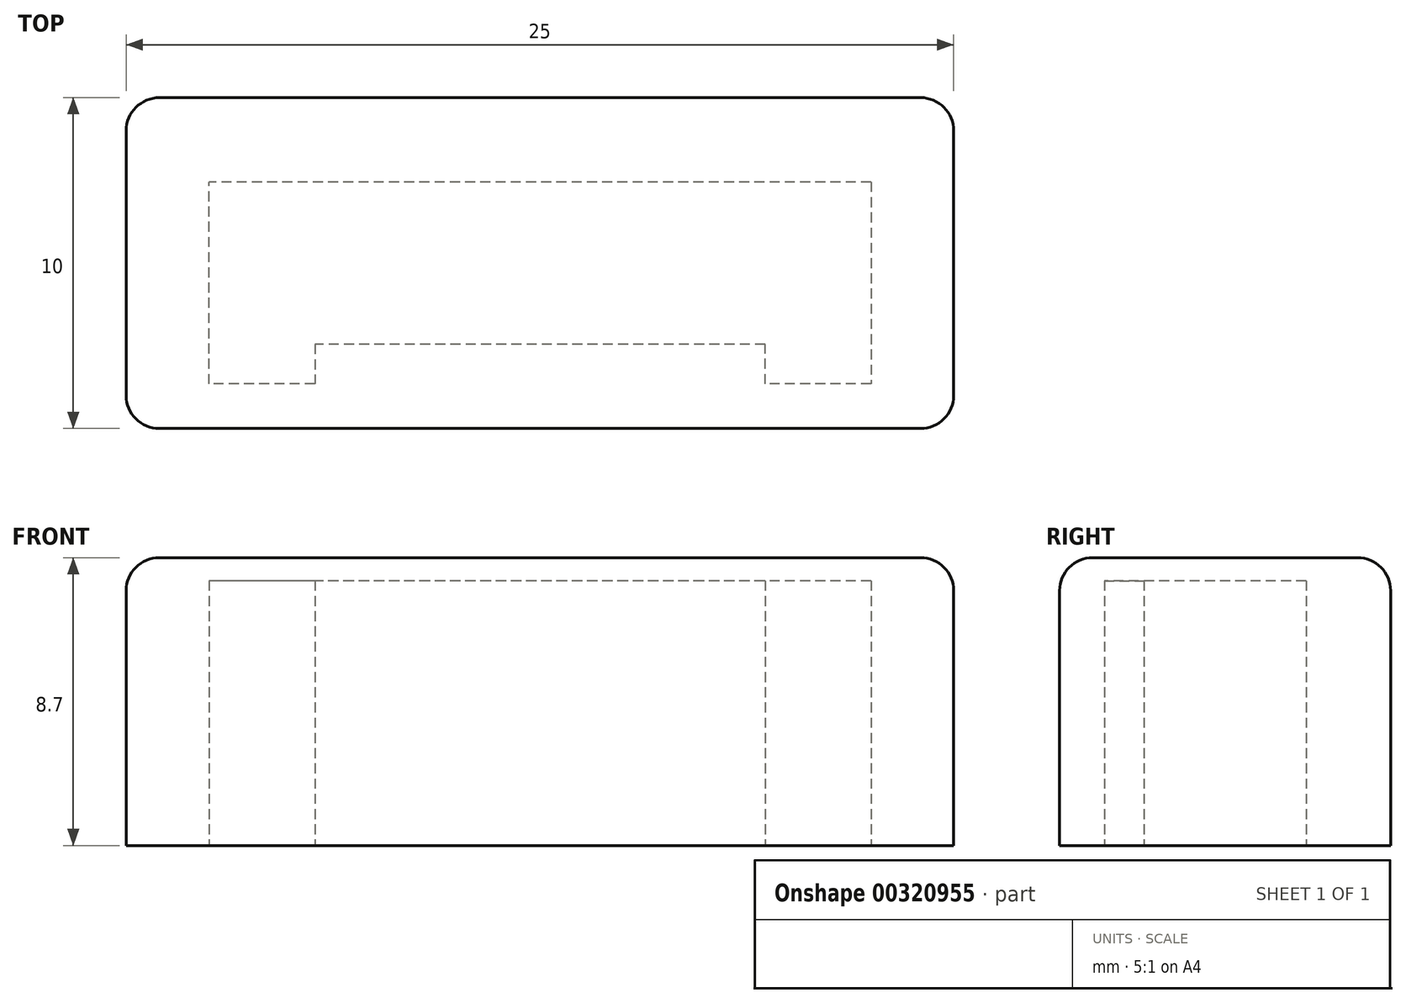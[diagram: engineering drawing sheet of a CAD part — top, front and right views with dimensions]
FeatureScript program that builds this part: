
annotation { "Feature Type Name" : "Feature", "Feature Type Description" : "" }
export const myFeature = defineFeature(function(context is Context, id is Id, definition is map)
    precondition{}
    {
        {
            var Q0;
            Q0=qCreatedBy(makeId("Top.planeOp"),FACE);
            var sketch = newSketch(context, id + "F0", { "sketchPlane" : qUnion([Q0])});
            skLineSegment(sketch, "E0.bottom", {"start": v(10, 2.45) * mm, "end": v(-10, 2.45) * mm});
            skLineSegment(sketch, "E0.top", {"start": v(10, -2.45) * mm, "end": v(-10, -2.45) * mm});
            skLineSegment(sketch, "E0.left", {"start": v(10, 2.45) * mm, "end": v(10, -2.45) * mm});
            skLineSegment(sketch, "E0.right", {"start": v(-10, 2.45) * mm, "end": v(-10, -2.45) * mm});
            skPoint(sketch, "E0.middle", {"position": v(0, 0) * mm});
            skLineSegment(sketch, "E1.bottom", {"start": v(12.5, -5) * mm, "end": v(-12.5, -5) * mm});
            skLineSegment(sketch, "E1.top", {"start": v(12.5, 5) * mm, "end": v(-12.5, 5) * mm});
            skLineSegment(sketch, "E1.left", {"start": v(12.5, -5) * mm, "end": v(12.5, 5) * mm});
            skLineSegment(sketch, "E1.right", {"start": v(-12.5, -5) * mm, "end": v(-12.5, 5) * mm});
            skLineSegment(sketch, "E2", {"start": v(10, -2.45) * mm, "end": v(10, -3.65) * mm});
            skLineSegment(sketch, "E3", {"start": v(10, -3.65) * mm, "end": v(6.8, -3.65) * mm});
            skLineSegment(sketch, "E4", {"start": v(6.8, -3.65) * mm, "end": v(6.8, -2.45) * mm});
            skLineSegment(sketch, "E5", {"start": v(6.8, -2.45) * mm, "end": v(10, -2.45) * mm});
            skLineSegment(sketch, "E6", {"start": v(-10, -2.45) * mm, "end": v(-6.8, -2.45) * mm});
            skLineSegment(sketch, "E7", {"start": v(-6.8, -2.45) * mm, "end": v(-6.8, -3.65) * mm});
            skLineSegment(sketch, "E8", {"start": v(-6.8, -3.65) * mm, "end": v(-10, -3.65) * mm});
            skLineSegment(sketch, "E9", {"start": v(-10, -3.65) * mm, "end": v(-10, -2.45) * mm});
            skSolve(sketch);
        }
        {
            var Q0;
            Q0 = qSketchRegion(id + "F0", true);
            extrude(context, id + "F1", {"entities" : qUnion([Q0]), "depth" : 8 * mm});
        }
        {
            var Q0;
            Q0=makeQuery(id+"F1.opExtrude","CAP_FACE",FACE,{"disambiguationData":[OSD([sQuery(id+"F0.wireOp",EDGE,"E0.bottom"),sQuery(id+"F0.wireOp",EDGE,"E0.top"),sQuery(id+"F0.wireOp",EDGE,"E0.left"),sQuery(id+"F0.wireOp",EDGE,"E0.right"),sQuery(id+"F0.wireOp",EDGE,"E1.bottom"),sQuery(id+"F0.wireOp",EDGE,"E1.top"),sQuery(id+"F0.wireOp",EDGE,"E1.left"),sQuery(id+"F0.wireOp",EDGE,"E1.right"),sQuery(id+"F0.wireOp",EDGE,"E2"),sQuery(id+"F0.wireOp",EDGE,"E3"),sQuery(id+"F0.wireOp",EDGE,"E4"),sQuery(id+"F0.wireOp",EDGE,"E7"),sQuery(id+"F0.wireOp",EDGE,"E8"),sQuery(id+"F0.wireOp",EDGE,"E9")])],"isStart":false});
            var sketch = newSketch(context, id + "F2", { "sketchPlane" : qUnion([Q0])});
            skLineSegment(sketch, "E10.bottom", {"start": v(-12.5, 5) * mm, "end": v(12.5, 5) * mm});
            skLineSegment(sketch, "E10.top", {"start": v(-12.5, -5) * mm, "end": v(12.5, -5) * mm});
            skLineSegment(sketch, "E10.left", {"start": v(-12.5, 5) * mm, "end": v(-12.5, -5) * mm});
            skLineSegment(sketch, "E10.right", {"start": v(12.5, 5) * mm, "end": v(12.5, -5) * mm});
            skPoint(sketch, "E10.middle", {"position": v(0, 0) * mm});
            skSolve(sketch);
        }
        {
            var Q0;
            Q0 = qSketchRegion(id + "F2", true);
            extrude(context, id + "F3", {"entities" : qUnion([Q0]), "operationType" : NewBodyOperationType.ADD, "depth" : .7 * mm});
        }
        {
            var Q0;
            Q0=makeQuery(id+"F3.opExtrude","CAP_FACE",FACE,{"disambiguationData":[OSD([sQuery(id+"F2.wireOp",EDGE,"E10.bottom"),sQuery(id+"F2.wireOp",EDGE,"E10.top"),sQuery(id+"F2.wireOp",EDGE,"E10.left"),sQuery(id+"F2.wireOp",EDGE,"E10.right")])],"isStart":false});
            fillet(context, id + "F4", {"entities" : qUnion([Q0]), "radius" : 1 * mm, "tangentPropagation" : true, "allowEdgeOverflow" : false});
        }
        {
            var Q0;
            Q0=makeQuery(id+"F3.boolean.opBoolean","MERGE",EDGE,{"derivedFrom":[makeQuery(id+"F1.opExtrude","SWEPT_EDGE",EDGE,{"disambiguationData":[OSD([sQuery(id+"F0.wireOp",EDGE,"E1.top"),sQuery(id+"F0.wireOp",EDGE,"E1.left")])]}),makeQuery(id+"F3.opExtrude","SWEPT_EDGE",EDGE,{"disambiguationData":[OSD([sQuery(id+"F2.wireOp",EDGE,"E10.bottom"),sQuery(id+"F2.wireOp",EDGE,"E10.right")])]})]});
            fillet(context, id + "F5", {"entities" : qUnion([Q0]), "radius" : 1 * mm, "tangentPropagation" : true, "allowEdgeOverflow" : false});
        }
        {
            var Q0;
            Q0=makeQuery(id+"F3.boolean.opBoolean","MERGE",EDGE,{"derivedFrom":[makeQuery(id+"F1.opExtrude","SWEPT_EDGE",EDGE,{"disambiguationData":[OSD([sQuery(id+"F0.wireOp",EDGE,"E1.top"),sQuery(id+"F0.wireOp",EDGE,"E1.right")])]}),makeQuery(id+"F3.opExtrude","SWEPT_EDGE",EDGE,{"disambiguationData":[OSD([sQuery(id+"F2.wireOp",EDGE,"E10.bottom"),sQuery(id+"F2.wireOp",EDGE,"E10.left")])]})]});
            var Q1;
            Q1=makeQuery(id+"F3.boolean.opBoolean","MERGE",EDGE,{"derivedFrom":[makeQuery(id+"F1.opExtrude","SWEPT_EDGE",EDGE,{"disambiguationData":[OSD([sQuery(id+"F0.wireOp",EDGE,"E1.bottom"),sQuery(id+"F0.wireOp",EDGE,"E1.left")])]}),makeQuery(id+"F3.opExtrude","SWEPT_EDGE",EDGE,{"disambiguationData":[OSD([sQuery(id+"F2.wireOp",EDGE,"E10.top"),sQuery(id+"F2.wireOp",EDGE,"E10.right")])]})]});
            var Q2;
            Q2=makeQuery(id+"F3.boolean.opBoolean","MERGE",EDGE,{"derivedFrom":[makeQuery(id+"F1.opExtrude","SWEPT_EDGE",EDGE,{"disambiguationData":[OSD([sQuery(id+"F0.wireOp",EDGE,"E1.bottom"),sQuery(id+"F0.wireOp",EDGE,"E1.right")])]}),makeQuery(id+"F3.opExtrude","SWEPT_EDGE",EDGE,{"disambiguationData":[OSD([sQuery(id+"F2.wireOp",EDGE,"E10.top"),sQuery(id+"F2.wireOp",EDGE,"E10.left")])]})]});
            fillet(context, id + "F6", {"entities" : qUnion([Q0, Q1, Q2]), "radius" : 1 * mm, "tangentPropagation" : true, "allowEdgeOverflow" : false});
        }
    });
